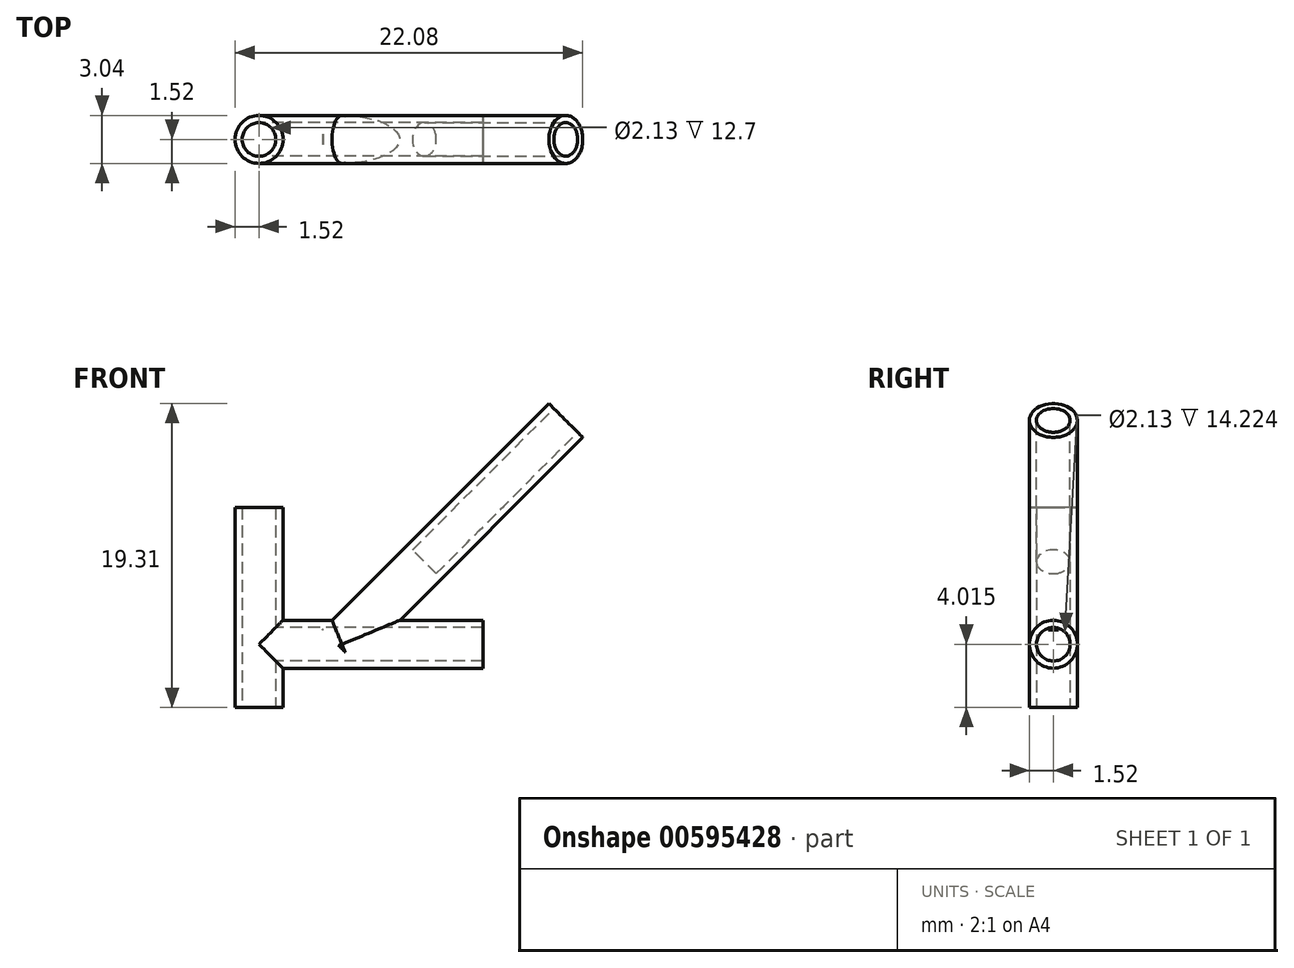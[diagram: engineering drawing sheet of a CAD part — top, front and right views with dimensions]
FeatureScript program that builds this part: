
annotation { "Feature Type Name" : "Feature", "Feature Type Description" : "" }
export const myFeature = defineFeature(function(context is Context, id is Id, definition is map)
    precondition{}
    {
        {
            var Q0;
            Q0=qCreatedBy(makeId("Top.planeOp"),FACE);
            var sketch = newSketch(context, id + "F0", { "sketchPlane" : qUnion([Q0])});
            skCircle(sketch, "E0", {"center": v(0, 0) * mm, "radius": 1.52 * mm});
            skCircle(sketch, "E1", {"center": v(0, 0) * mm, "radius": 1.07 * mm});
            skSolve(sketch);
        }
        {
            var Q0;
            Q0=makeQuery(id+"F0.imprint","IMPRINT",FACE,{"disambiguationData":[TD([[makeQuery(id+"F0.imprint","IMPRINT",EDGE,{"derivedFrom":sQuery(id+"F0.wireOp",EDGE,"E0")}),1.0]])]});
            extrude(context, id + "F1", {"entities" : qUnion([Q0]), "depth" : 12.7 * mm, "offsetDistance" : 25.4 * mm});
        }
        {
            var Q0;
            Q0=qCreatedBy(makeId("Right.planeOp"),FACE);
            cPlane(context, id + "F2", {"entities" : qUnion([Q0]), "cplaneType" : CPlaneType.OFFSET, "offset" : 1.52 * mm, "width" : 152.4 * mm, "height" : 152.4 * mm});
        }
        {
            var Q0;
            Q0=qCreatedBy(id+"F2.planeOp",FACE);
            var sketch = newSketch(context, id + "F3", { "sketchPlane" : qUnion([Q0])});
            skCircle(sketch, "E2", {"center": v(0, 4.02) * mm, "radius": 1.52 * mm});
            skSolve(sketch);
        }
        {
            var Q0;
            Q0=makeQuery(id+"F3.imprint","IMPRINT",FACE,{"disambiguationData":[TD([[makeQuery(id+"F3.imprint","IMPRINT",EDGE,{"derivedFrom":sQuery(id+"F3.wireOp",EDGE,"E2")}),1.0]])]});
            extrude(context, id + "F4", {"entities" : qUnion([Q0]), "operationType" : NewBodyOperationType.ADD, "oppositeDirection" : true, "depth" : 1.52 * mm, "offsetDistance" : 25.4 * mm});
        }
        {
            var Q0;
            Q0=makeQuery(id+"F4.opExtrude","CAP_FACE",FACE,{"disambiguationData":[OSD([sQuery(id+"F3.wireOp",EDGE,"E2")])],"isStart":true});
            var sketch = newSketch(context, id + "F5", { "sketchPlane" : qUnion([Q0])});
            skCircle(sketch, "E3", {"center": v(0, 4.02) * mm, "radius": 1.52 * mm});
            skCircle(sketch, "E4", {"center": v(0, 4.02) * mm, "radius": 1.07 * mm});
            skSolve(sketch);
        }
        {
            var Q0;
            Q0=makeQuery(id+"F5.imprint","IMPRINT",FACE,{"disambiguationData":[TD([[makeQuery(id+"F5.imprint","IMPRINT",EDGE,{"derivedFrom":sQuery(id+"F5.wireOp",EDGE,"E4")}),-1.0]])]});
            extrude(context, id + "F6", {"entities" : qUnion([Q0]), "operationType" : NewBodyOperationType.ADD, "depth" : 12.7 * mm, "offsetDistance" : 25.4 * mm});
        }
        {
            var Q0;
            Q0=makeQuery(id+"F4.opExtrude","CAP_FACE",FACE,{"disambiguationData":[OSD([sQuery(id+"F3.wireOp",EDGE,"E2")])],"isStart":false});
            var sketch = newSketch(context, id + "F7", { "sketchPlane" : qUnion([Q0])});
            skCircle(sketch, "E5", {"center": v(0, 4.02) * mm, "radius": 1.07 * mm});
            skSolve(sketch);
        }
        {
            var Q0;
            Q0 = qSketchRegion(id + "F7", true);
            extrude(context, id + "F8", {"entities" : qUnion([Q0]), "operationType" : NewBodyOperationType.REMOVE, "oppositeDirection" : true, "depth" : 12.7 * mm, "offsetDistance" : 25.4 * mm});
        }
        {
            var Q0;
            Q0=makeQuery(id+"F1.opExtrude","CAP_FACE",FACE,{"disambiguationData":[OSD([sQuery(id+"F0.wireOp",EDGE,"E0"),sQuery(id+"F0.wireOp",EDGE,"E1")])],"isStart":false});
            var sketch = newSketch(context, id + "F9", { "sketchPlane" : qUnion([Q0])});
            skCircle(sketch, "E6", {"center": v(0, 0) * mm, "radius": 1.07 * mm});
            skSolve(sketch);
        }
        {
            var Q0;
            Q0 = qSketchRegion(id + "F9", true);
            extrude(context, id + "F10", {"entities" : qUnion([Q0]), "operationType" : NewBodyOperationType.REMOVE, "oppositeDirection" : true, "depth" : 25.4 * mm, "offsetDistance" : 25.4 * mm});
        }
        {
            var Q0;
            Q0=qCreatedBy(makeId("Right.planeOp"),FACE);
            var Q1;
            Q1=qCreatedBy(makeId("Top.planeOp"),FACE);
            cPlane(context, id + "F11", {"entities" : qUnion([Q0, Q1]), "cplaneType" : CPlaneType.MID_PLANE, "offset" : 25.4 * mm, "oppositeDirection" : true, "flipAlignment" : true, "width" : 152.4 * mm, "height" : 152.4 * mm});
        }
        {
            var Q0;
            Q0=qCreatedBy(id+"F11.planeOp",FACE);
            cPlane(context, id + "F12", {"entities" : qUnion([Q0]), "cplaneType" : CPlaneType.OFFSET, "offset" : 6.35 * mm, "width" : 152.4 * mm, "height" : 152.4 * mm});
        }
        {
            var Q0;
            Q0=qCreatedBy(id+"F12.planeOp",FACE);
            var sketch = newSketch(context, id + "F13", { "sketchPlane" : qUnion([Q0])});
            skCircle(sketch, "E7", {"center": v(0, -0.89) * mm, "radius": 1.52 * mm});
            skSolve(sketch);
        }
        {
            var Q0;
            Q0 = qSketchRegion(id + "F13", true);
            extrude(context, id + "F14", {"entities" : qUnion([Q0]), "operationType" : NewBodyOperationType.ADD, "depth" : 20.32 * mm, "offsetDistance" : 25.4 * mm});
        }
        {
            var Q0;
            Q0=makeQuery(id+"F14.opExtrude","CAP_FACE",FACE,{"disambiguationData":[OSD([sQuery(id+"F13.wireOp",EDGE,"E7")])],"isStart":false});
            var sketch = newSketch(context, id + "F15", { "sketchPlane" : qUnion([Q0])});
            skCircle(sketch, "E8", {"center": v(0, -0.89) * mm, "radius": 1.07 * mm});
            skSolve(sketch);
        }
        {
            var Q0;
            Q0 = qSketchRegion(id + "F15", true);
            extrude(context, id + "F16", {"entities" : qUnion([Q0]), "operationType" : NewBodyOperationType.REMOVE, "oppositeDirection" : true, "depth" : 12.7 * mm, "offsetDistance" : 25.4 * mm});
        }
        {
            var Q0;
            Q0=makeQuery(id+"F6.opExtrude","CAP_FACE",FACE,{"disambiguationData":[OSD([sQuery(id+"F5.wireOp",EDGE,"E3"),sQuery(id+"F5.wireOp",EDGE,"E4")])],"isStart":false});
            var sketch = newSketch(context, id + "F17", { "sketchPlane" : qUnion([Q0])});
            skCircle(sketch, "E9", {"center": v(0, 4.02) * mm, "radius": 1.07 * mm});
            skSolve(sketch);
        }
        {
            var Q0;
            Q0=makeQuery(id+"F17.imprint","IMPRINT",FACE,{"disambiguationData":[TD([[makeQuery(id+"F17.imprint","IMPRINT",EDGE,{"derivedFrom":sQuery(id+"F17.wireOp",EDGE,"E9")}),1.0]])]});
            extrude(context, id + "F18", {"entities" : qUnion([Q0]), "operationType" : NewBodyOperationType.REMOVE, "oppositeDirection" : true, "depth" : 10.16 * mm, "offsetDistance" : 25.4 * mm});
        }
        {
            var Q0;
            Q0=qCreatedBy(id+"F2.planeOp",FACE);
            var sketch = newSketch(context, id + "F19", { "sketchPlane" : qUnion([Q0])});
            skCircle(sketch, "E10", {"center": v(0, 4.02) * mm, "radius": 1.07 * mm});
            skCircle(sketch, "E11", {"center": v(0, 4.02) * mm, "radius": 1.52 * mm});
            skSolve(sketch);
        }
        {
            var Q0;
            Q0 = qSketchRegion(id + "F19", true);
            extrude(context, id + "F20", {"entities" : qUnion([Q0]), "operationType" : NewBodyOperationType.ADD, "depth" : 12.7 * mm, "offsetDistance" : 25.4 * mm});
        }
        {
            var Q0;
            Q0=makeQuery(id+"F14.opExtrude","CAP_FACE",FACE,{"disambiguationData":[OSD([sQuery(id+"F13.wireOp",EDGE,"E7")])],"isStart":false});
            var sketch = newSketch(context, id + "F21", { "sketchPlane" : qUnion([Q0])});
            skCircle(sketch, "E12", {"center": v(0, -0.89) * mm, "radius": 1.07 * mm});
            skSolve(sketch);
        }
        {
            var Q0;
            Q0=makeQuery(id+"F21.imprint","IMPRINT",FACE,{"disambiguationData":[TD([[makeQuery(id+"F21.imprint","IMPRINT",EDGE,{"derivedFrom":sQuery(id+"F21.wireOp",EDGE,"E12")}),1.0]])]});
            extrude(context, id + "F22", {"entities" : qUnion([Q0]), "operationType" : NewBodyOperationType.REMOVE, "oppositeDirection" : true, "depth" : 12.45 * mm, "offsetDistance" : 25.4 * mm});
        }
    });
